# Revit family: Gleitplatte 2x 1-2 Zoll
name_source: partatom
category: HLS-Bauteile
revit_build: Autodesk Revit 2017 (Build: 20190507_1515(x64)
units: mm (PartAtom-declared; Revit-internal decimal feet)

## family parameters
Arbeitsebenenbasiert = Ja
Beim Laden mit Abzugskörper schneiden = Nein
Bemaßung runder Anschluss = Durchmesser verwenden
Gemeinsam genutzt = Ja
Immer vertikal = Nein
OmniClass-Nummer = 23.75.00.00
OmniClass-Titel = Climate Control (HVAC)
Raumberechnungspunkt = Nein
Teiletyp = Normal

## types (6) — shared parameters
Abstand zur Außenkante = 25 mm  [stored 0.082021 ft]
Achsmaß = 25 mm
Anschlüsse = Runde Gewindeanschlusse parametrik : Muffe 1/2´´ (0009865)
Anzahl Anschlüsse = 2
Fabrikat = MEFA
Firma = MEFA Befestigungs- und Montagesysteme GmbH
Mengeneinheit = St
vpe = 1 St
zero-valued in all types: Vorgabe-Ansicht

## per-type parameters (varying)
| type | Anschluss | Artikelnummer | Breite | EAN | Gewicht | Gewicht pro Bauteil | Höhe Gewindeanschluss HGW | Kurztext1 | Kurztext2 | Länge | Stärke | max. zul. Last |
| Gleitplatte 200x100x 8, 2x 1/2" | 1/2´´ | 0771811 | 100 mm  [stored 0.328084 ft] | 4250928418364 | 4.95 kg | 4.95 kg | 20 mm  [stored 0.0656168 ft] | Gleitplatte 300 x 200 x 10 | Anschluss 2 x 1'' | 200 mm  [stored 0.656168 ft] | 10 mm  [stored 0.0328084 ft] | 5.60 kN |
| Gleitplatte 200x150x 8, 2x 1/2" | 1/2'' | 0771331 | 150 mm | 4250928418296 | 1.98 kg | 1.98 kg | 15 mm  [stored 0.0492126 ft] | Gleitplatte 200 x 150 x 8 | Anschluss 2 x 1/2'' | 200 mm  [stored 0.656168 ft] | 8 mm  [stored 0.0262467 ft] | 4.40 kN |
| Gleitplatte 250x100x 8, 2x 1/2" | 1/2'' | 0771503 | 100 mm  [stored 0.328084 ft] | 4250928418319 | 1.66 kg | 1.66 kg | 15 mm  [stored 0.0492126 ft] | Gleitplatte 250 x 100 x 8 | Anschluss 2 x 1/2'' | 250 mm | 8 mm  [stored 0.0262467 ft] | 2.20 kN |
| Gleitplatte 250x200x10, 2x 1/2" | 1/2'' | 0771710 | 200 mm  [stored 0.656168 ft] | 4250928418357 | 4.06 kg | 4.06 kg | 15 mm  [stored 0.0492126 ft] | Gleitplatte 250 x 200 x 10 | Anschluss 2 x 1/2'' | 250 mm | 10 mm  [stored 0.0328084 ft] | 6.40 kN |
| Gleitplatte 150x100x 8, 2x 1/2" | 1/2'' | 0771202 | 100 mm  [stored 0.328084 ft] | 4250928418241 | 1.02 kg | 1.02 kg | 15 mm  [stored 0.0492126 ft] | Gleitplatte 150 x 100 x 8 | Anschluss 2 x 1/2'' | 150 mm | 8 mm  [stored 0.0262467 ft] | 4.80 kN |
| Gleitplatte 250x200x 8, 2x 1/2" | 1/2'' | 0771707 | 200 mm  [stored 0.656168 ft] | 4250928418340 | 3.26 kg | 3.26 kg | 15 mm  [stored 0.0492126 ft] | Gleitplatte 250 x 200 x 8 | Anschluss 2 x 1/2'' | 250 mm | 8 mm  [stored 0.0262467 ft] | 4.20 kN |

note: [stored X ft] marks values corroborated as IEEE doubles in the binary element streams (Revit-internal decimal feet)

## geometry (parser evidence)
native form markers: Sweep x1
no freeform markers — native parametric forms only
